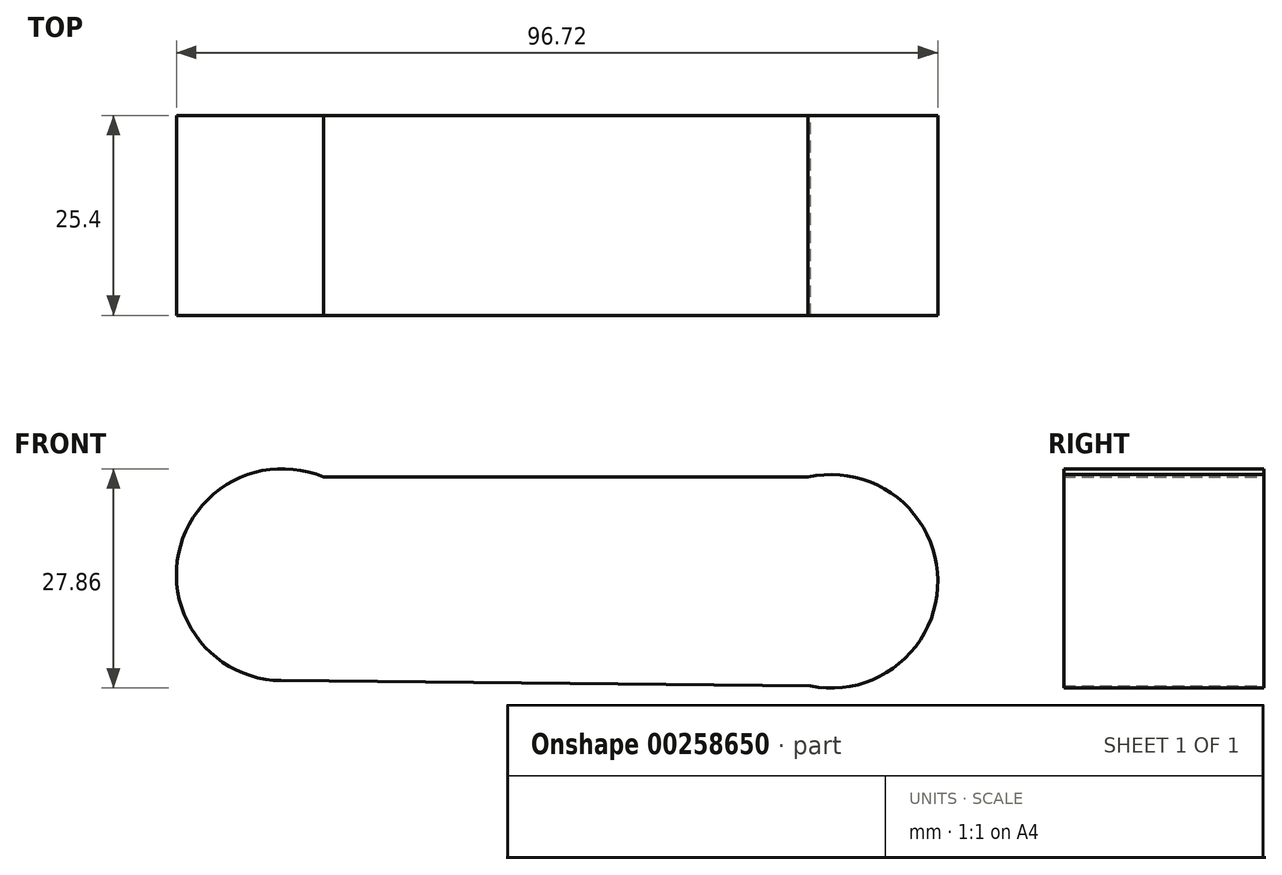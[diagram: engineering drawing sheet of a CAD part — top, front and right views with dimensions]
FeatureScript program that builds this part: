
annotation { "Feature Type Name" : "Feature", "Feature Type Description" : "" }
export const myFeature = defineFeature(function(context is Context, id is Id, definition is map)
    precondition{}
    {
        {
            var Q0;
            Q0=qCreatedBy(makeId("Front.planeOp"),FACE);
            var sketch = newSketch(context, id + "F0", { "sketchPlane" : qUnion([Q0])});
            skArc(sketch, "E0", {"start": v(32.45, 2.65) * mm, "mid": v(48.62, 16.12) * mm, "end": v(32.14, 29.22) * mm});
            skArc(sketch, "E1", {"start": v(-29.44, 29.22) * mm, "mid": v(-47.82, 19.54) * mm, "end": v(-34.79, 3.36) * mm});
            skLineSegment(sketch, "E2", {"start": v(32.14, 29.22) * mm, "end": v(-29.44, 29.22) * mm});
            skLineSegment(sketch, "E3", {"start": v(32.45, 2.65) * mm, "end": v(-34.79, 3.36) * mm});
            skSolve(sketch);
        }
        {
            var Q0;
            Q0=makeQuery(id+"F0.imprint","IMPRINT",FACE,{"disambiguationData":[TD([[makeQuery(id+"F0.imprint","IMPRINT",EDGE,{"derivedFrom":sQuery(id+"F0.wireOp",EDGE,"E0")}),1.0]])]});
            var Q1;
            Q1 = qSketchRegion(id + "F0", true);
            extrude(context, id + "F1", {"entities" : qUnion([Q0, Q1]), "depth" : 25.4 * mm});
        }
    });
